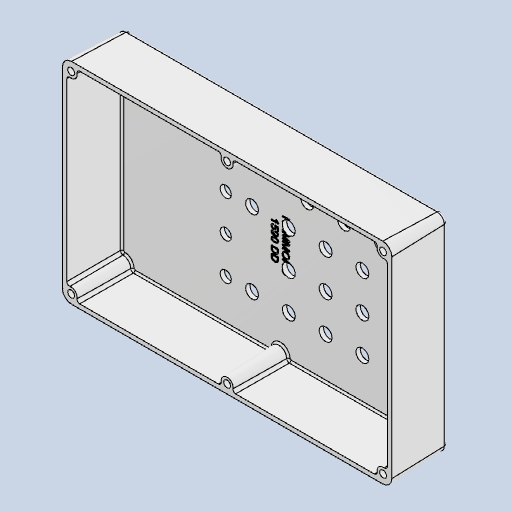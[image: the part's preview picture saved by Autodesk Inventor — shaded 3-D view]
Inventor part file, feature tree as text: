
AUTODESK INVENTOR PART (.ipt)
format: ipt  version: 2022.2 (Build 262287000, 287)  size: 611,840 bytes
history: native  units: in
note: dims shown in document units (in); Inventor stores cm internally (conversion verified against a paired STEP export)
features: extrude x1, sketch x1
ambient origin geometry x8: Origin, YZ Plane, XZ Plane, XY Plane, X Axis, Y Axis, Z Axis, Center Point
bodies: Solid2 (feature_tree), Solid1 (feature_tree)
feature tree (2):
  extrude  "Extrusion1"  Depth=0.3937in
  sketch  "Sketch1"  dims[d8=0.254in d9=0.2913in d10=0.27in d11=0.65in d12=0.7874in d13=0.7874in d14=1.5748in d16=0.8268in d17=0.3937in d19=0.3937in d21=0.5in d22=0.375in d23=0.2913in d24=0.7874in d25=1.9685in d27=0.8268in d28=0.3937in d30=0.3937in d33=0.0394in d34=0.2913in d35=0.7874in d36=1.5748in d38=0.8268in d39=0.3937in d41=0.3937in d43=0.5906in d44=0.7874in d46=1.6535in d47=0.3937in d49=0.3937in d51=0.5906in d52=0.254in d53=0.8268in d54=0.5906in d55=1.5748in d56=0.3937in d57=0.0in]
